# Revit family: ElectricalEquipment_Hager_TPNLighting&Power_HagerTPNExtBox(withdoor)
name_source: partatom
category: Electrical Equipment
revit_build: Autodesk Revit 2015 (Build: 20160512_1515(x64)
units: mm (PartAtom-declared; Revit-internal decimal feet)

## types (1)
- TPN JK1 Ext Box Dinrail Side (04W)
    Busbar Rating = 100 A
    CE Approval = Yes
    Colour = BS4800:2011 00A01 Oyster Grey
    Default Elevation = 1200 mm
    Description = Invicta 3 TPN JK1 Dinrail 2 Row (4W) Glazed Door
    Design Country = China
    Door = 46 mm  [stored 0.150919 ft]
    Door Type = Single Glazed Door
    EAN = 5015652257974
    Enclosure Rating = IP3X
    Frequency = 50 Hz
    Hager Catalogue Ref = JK104BDFG
    Location = Indoors
    Location of Manufacturer = Telford, TF1 7FT
    MCB Rating = 63 A
    Mains Type = 1 phase
    Manufacturer = Hager UK Ltd
    Manufacturer Country = United Kingdom
    Manufacturer Website = www.hager.co.uk
    Model = JK104BDFG
    Modules = 32
    Neutral Rating = 100.00%
    Number of Poles = 2
    Overall Height = 133 mm  [stored 0.436352 ft]
    Overall Width = 465 mm  [stored 1.52559 ft]
    Packaging Recyclable = Yes
    Packaging Weight = 0.50 kg
    Pollution Degree = 2
    Product Description = Invicta 3 TPN JK1 Dinrail 2 Row (4W) Glazed Door
    Product Family = TPN JK1 Ext Box Dinrail Side (04W)
    Product Group = TPN
    Product Literature = www.hager.co.uk/?artnr=JK104BDFG
    Product Range = Invicta 3 TPN JK1 Dinrail 2 Row (4W)
    Product Weight = 8.80 kg
    Reference Standard = BS EN 62208
    Revision = 2
    Shape = Rectangular
    Supply Phase = 1
    Type = ElectricalFixture
    Type Comments = Mounted on LHS or RHS of DB or free standing
    URL = www.hager.co.uk
    Ui Rating = 690 V
    Voltage = 230
    Warranty ID = 24 Months

note: [stored X ft] marks values corroborated as IEEE doubles in the binary element streams (Revit-internal decimal feet)

## geometry (parser evidence)
native form markers: Sweep x3
no freeform markers — native parametric forms only
